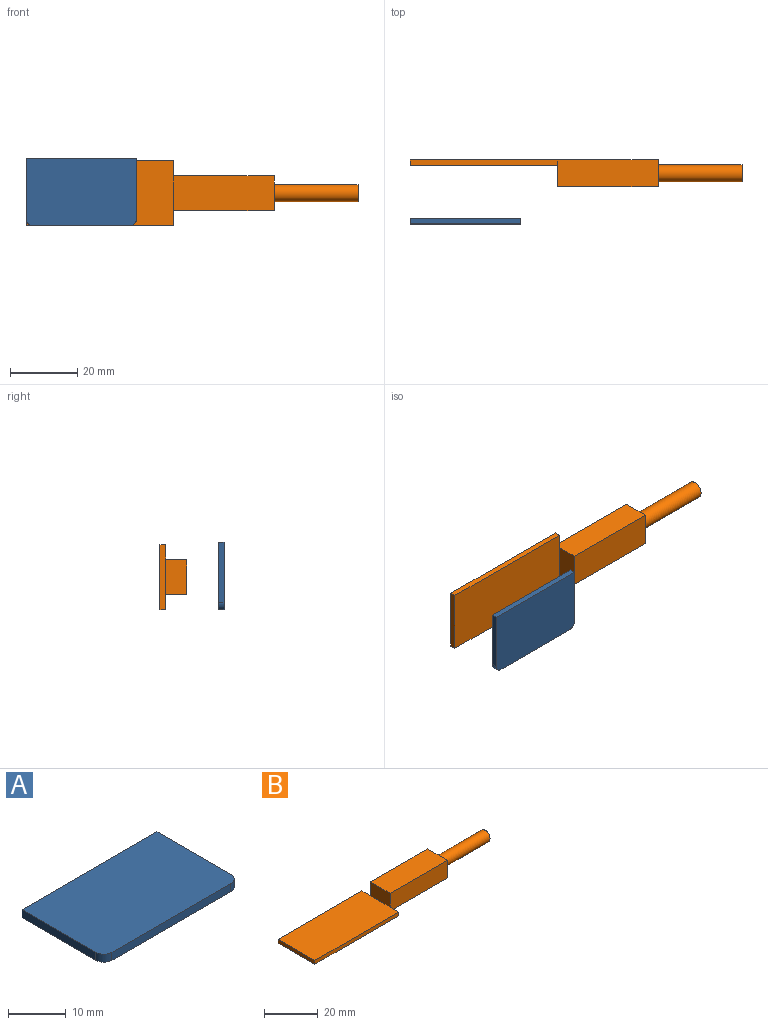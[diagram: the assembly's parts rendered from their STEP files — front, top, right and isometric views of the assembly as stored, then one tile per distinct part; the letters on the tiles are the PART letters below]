
ASSEMBLY  parts=2 mates=2
PART A: 8 faces, bbox 33x20x1.7 mm
  f0: plane 18x1.7mm, normal (1,0,0), area 30.6mm2, adj f1,f5,f6,f7
  f1: plane 33x1.7mm, normal (0,1,0), area 56.1mm2, adj f0,f2,f6,f7
  f2: plane 18x1.7mm, normal (-1,0,0), area 30.6mm2, adj f1,f3,f6,f7
  f3: cylinder r=2mm len=2mm, axis (0,0,-1), area 5.3mm2, adj f2,f4,f6,f7
  f4: plane 29x1.7mm, normal (0,-1,0), area 49.3mm2, adj f3,f5,f6,f7
  f5: cylinder r=2mm len=2mm, axis (0,0,-1), area 5.3mm2, adj f0,f4,f6,f7
  f6: plane 33x20mm, normal (0,0,1), area 658.3mm2, adj f0,f1,f2,f3,f4,f5
  f7: plane 33x20mm, normal (0,0,-1), area 658.3mm2, adj f0,f1,f2,f3,f4,f5
PART B: 14 faces, bbox 99x19.3x8 mm
  f0: plane 4.48x1.7mm, normal (1,0,0), area 7.6mm2, adj f2,f5,f6,f8
  f1: plane 4.48x1.7mm, normal (1,0,0), area 7.6mm2, adj f4,f5,f6,f9
  f2: plane 44x1.7mm, normal (0,1,0), area 74.8mm2, adj f0,f3,f5,f6
  f3: plane 19.28x1.7mm, normal (-1,0,0), area 32.8mm2, adj f2,f4,f5,f6
  f4: plane 44x1.7mm, normal (0,-1,0), area 74.8mm2, adj f1,f3,f5,f6
  f5: plane 44x19.28mm, normal (0,0,1), area 848.4mm2, adj f0,f1,f2,f3,f4,f7
  f6: plane 74x19.28mm, normal (0,0,-1), area 1157.9mm2, adj f0,f1,f2,f3,f4,f8,f9,f10
  f7: plane 10.32x6.3mm, normal (-1,0,0), area 65mm2, adj f5,f8,f9,f11
  f8: plane 30x8mm, normal (0,1,0), area 240mm2, adj f0,f6,f7,f10,f11
  f9: plane 30x8mm, normal (0,-1,0), area 240mm2, adj f1,f6,f7,f10,f11
  f10: plane 10.32x8mm, normal (1,0,0), area 62.9mm2, adj f6,f8,f9,f11,f12
  f11: plane 30x10.32mm, normal (0,0,1), area 309.5mm2, adj f7,f8,f9,f10
  f12: cylinder r=2.5mm len=25mm, axis (-1,0,0), area 392.7mm2, adj f10,f13
  f13: plane 5x5mm, normal (1,0,0), area 19.6mm2, adj f12
PLACE A rot(axis=(1,0,0),90deg) t=(-99.08,24.57,23.18)mm
PLACE B rot(axis=(1,0,0),90deg) t=(-95.21,41.98,36.62)mm
MATE planar A.f4 <-> B.f4  axis (0,0,-1) through (-96.48,23.72,19.61)mm
MATE planar B.f3 <-> A.f2  axis (-1,0,0) through (-112.98,41.13,29.26)mm
